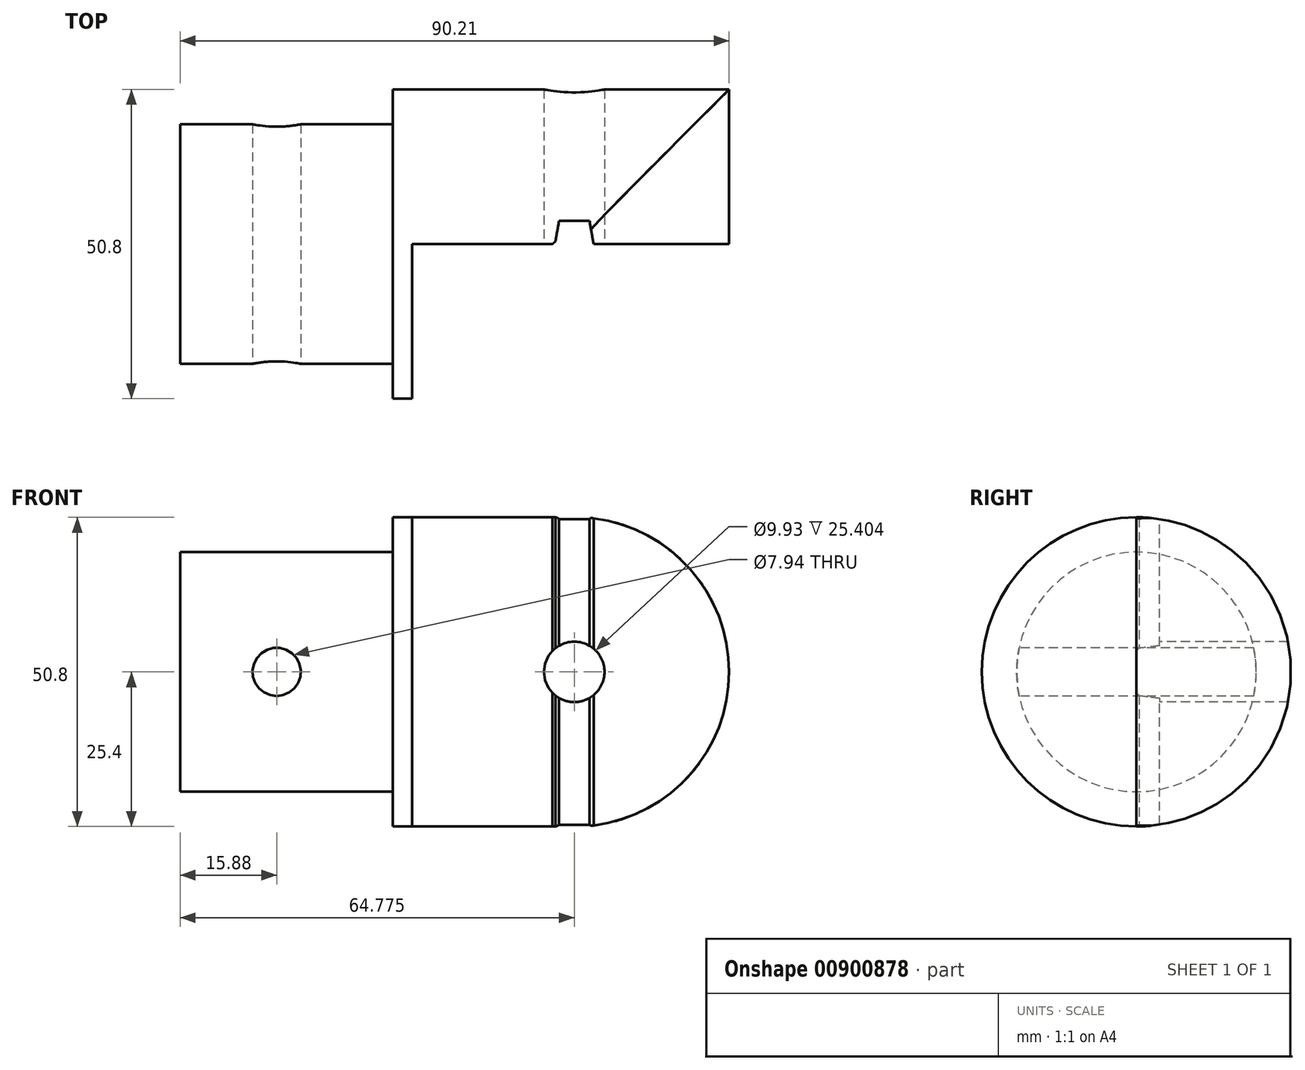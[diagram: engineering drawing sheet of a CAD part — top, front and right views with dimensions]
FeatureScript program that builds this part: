
annotation { "Feature Type Name" : "Feature", "Feature Type Description" : "" }
export const myFeature = defineFeature(function(context is Context, id is Id, definition is map)
    precondition{}
    {
        {
            var Q0;
            Q0=qCreatedBy(makeId("Right.planeOp"),FACE);
            var sketch = newSketch(context, id + "F0", { "sketchPlane" : qUnion([Q0])});
            skCircle(sketch, "E0", {"center": v(0, 0) * mm, "radius": 25.4 * mm});
            skSolve(sketch);
        }
        {
            var Q0;
            Q0=makeQuery(id+"F0.imprint","IMPRINT",FACE,{"disambiguationData":[TD([[makeQuery(id+"F0.imprint","IMPRINT",EDGE,{"derivedFrom":sQuery(id+"F0.wireOp",EDGE,"E0")}),1.0]])]});
            var Q1;
            Q1=sQuery(id+"F0.wireOp",EDGE,"E0");
            extrude(context, id + "F1", {"entities" : qUnion([Q0]), "surfaceEntities" : qUnion([Q1]), "depth" : 3.17 * mm, "offsetDistance" : 25.4 * mm});
        }
        {
            var Q0;
            Q0=makeQuery(id+"F1.opExtrude","CAP_FACE",FACE,{"disambiguationData":[OSD([sQuery(id+"F0.wireOp",EDGE,"E0")])],"isStart":false});
            var sketch = newSketch(context, id + "F2", { "sketchPlane" : qUnion([Q0])});
            skCircle(sketch, "E1", {"center": v(0, 0) * mm, "radius": 19.69 * mm});
            skSolve(sketch);
        }
        {
            var Q0;
            Q0 = qSketchRegion(id + "F2", true);
            extrude(context, id + "F3", {"entities" : qUnion([Q0]), "operationType" : NewBodyOperationType.ADD, "oppositeDirection" : true, "depth" : 38.1 * mm, "offsetDistance" : 25.4 * mm});
        }
        {
            var Q0;
            Q0=qCreatedBy(makeId("Right.planeOp"),FACE);
            var sketch = newSketch(context, id + "F4", { "sketchPlane" : qUnion([Q0])});
            skCircle(sketch, "E2.0", {"center": v(0, 0) * mm, "radius": 25.4 * mm});
            skSolve(sketch);
        }
        {
            var Q0;
            Q0 = qSketchRegion(id + "F4", true);
            extrude(context, id + "F5", {"entities" : qUnion([Q0]), "operationType" : NewBodyOperationType.ADD, "depth" : 58.42 * mm, "offsetDistance" : 25.4 * mm});
        }
        {
            var Q0;
            Q0=qCreatedBy(makeId("Front.planeOp"),FACE);
            var sketch = newSketch(context, id + "F6", { "sketchPlane" : qUnion([Q0])});
            skLineSegment(sketch, "E3", {"start": v(3.18, 25.4) * mm, "end": v(50.8, 25.4) * mm});
            skLineSegment(sketch, "E4", {"start": v(58.42, -25.4) * mm, "end": v(3.18, -25.4) * mm});
            skLineSegment(sketch, "E5.bottom", {"start": v(3.18, 25.4) * mm, "end": v(58.42, 25.4) * mm});
            skLineSegment(sketch, "E5.top", {"start": v(3.18, -25.4) * mm, "end": v(58.42, -25.4) * mm});
            skLineSegment(sketch, "E5.left", {"start": v(3.18, 25.4) * mm, "end": v(3.18, -25.4) * mm});
            skLineSegment(sketch, "E5.right", {"start": v(58.42, 25.4) * mm, "end": v(58.42, -25.4) * mm});
            skSolve(sketch);
        }
        {
            var Q0;
            Q0 = qSketchRegion(id + "F6", true);
            extrude(context, id + "F7", {"entities" : qUnion([Q0]), "operationType" : NewBodyOperationType.REMOVE, "endBound" : BoundingType.THROUGH_ALL, "depth" : 25.4 * mm, "offsetDistance" : 25.4 * mm});
        }
        {
            var Q0;
            Q0=makeQuery(id+"F7.boolean.opBoolean","COPY",FACE,{"derivedFrom":makeQuery(id+"F7.opExtrude","SWEPT_FACE",FACE,{"disambiguationData":[OSD([sQuery(id+"F6.wireOp",EDGE,"E5.left")])]})});
            cPlane(context, id + "F8", {"entities" : qUnion([Q0]), "cplaneType" : CPlaneType.OFFSET, "offset" : 26.67 * mm, "width" : 152.4 * mm, "height" : 152.4 * mm});
        }
        {
            var Q0;
            Q0=qCreatedBy(makeId("Front.planeOp"),FACE);
            var sketch = newSketch(context, id + "F9", { "sketchPlane" : qUnion([Q0])});
            skPoint(sketch, "E6", {"position": v(29.85, 0) * mm});
            skSolve(sketch);
        }
        {
            var Q0;
            Q0=sQuery(id+"F9.wireOp",VERTEX,"E6");
            var Q1;
            Q1=makeQuery(id+"F1.opExtrude","SWEPT_BODY",BODY,{"disambiguationData":[OSD([sQuery(id+"F0.wireOp",EDGE,"E0")])]});
            hole(context, id + "F10", {"style" : HoleStyle.SIMPLE, "endStyle" : HoleEndStyle.THROUGH, "standardTappedOrClearance" : lookupTablePath({ "fit" : "Close (ASME)", "standard" : "ANSI", "size" : "3/8", "type" : "Clearance" }), "standardBlindInLast" : lookupTablePath({ "fit" : "Close", "standard" : "ANSI", "size" : "3/8", "type" : "Clearance" }), "holeDiameter" : 9.93 * mm, "majorDiameter" : 9.52 * mm, "isTappedThrough" : true, "tappedDepth" : 12.7 * mm, "tapClearance" : 3, "locations" : qUnion([Q0]), "scope" : qUnion([Q1])});
        }
        {
            var Q0;
            Q0=qCreatedBy(makeId("Top.planeOp"),FACE);
            var sketch = newSketch(context, id + "F11", { "sketchPlane" : qUnion([Q0])});
            skLineSegment(sketch, "E7.left", {"start": v(26.67, 0) * mm, "end": v(33.02, 0) * mm});
            skLineSegment(sketch, "E7.right", {"start": v(27.34, 3.81) * mm, "end": v(32.35, 3.81) * mm});
            skLineSegment(sketch, "E8", {"start": v(26.67, 0) * mm, "end": v(27.34, 3.81) * mm});
            skLineSegment(sketch, "E9", {"start": v(33.02, 0) * mm, "end": v(32.35, 3.81) * mm});
            skLineSegment(sketch, "E10", {"start": v(29.85, 0) * mm, "end": v(29.85, 6.7) * mm, "construction": true});
            skSolve(sketch);
        }
        {
            var Q0;
            Q0 = qSketchRegion(id + "F11", true);
            var Q1;
            Q1=makeQuery(id+"F7.boolean.opBoolean","MERGE",FACE,{"derivedFrom":[makeQuery(id+"F1.opExtrude","CAP_FACE",FACE,{"disambiguationData":[OSD([sQuery(id+"F0.wireOp",EDGE,"E0")])],"isStart":false})],"fromTools":[makeQuery(id+"F7.opExtrude","SWEPT_FACE",FACE,{"disambiguationData":[OSD([sQuery(id+"F6.wireOp",EDGE,"E5.left")])]})]});
            extrude(context, id + "F12", {"entities" : qUnion([Q0]), "operationType" : NewBodyOperationType.REMOVE, "endBound" : BoundingType.SYMMETRIC, "oppositeDirection" : true, "depth" : 50.8 * mm, "endBoundEntityFace" : qUnion([Q1]), "offsetDistance" : 25.4 * mm});
        }
        {
            var Q0;
            Q0=qCreatedBy(makeId("Front.planeOp"),FACE);
            cPlane(context, id + "F13", {"entities" : qUnion([Q0]), "cplaneType" : CPlaneType.OFFSET, "offset" : 25.4 * mm, "width" : 152.4 * mm, "height" : 152.4 * mm});
        }
        {
            var Q0;
            Q0=qCreatedBy(id+"F13.planeOp",FACE);
            var sketch = newSketch(context, id + "F14", { "sketchPlane" : qUnion([Q0])});
            skPoint(sketch, "E11", {"position": v(29.85, 0) * mm});
            skPoint(sketch, "E12", {"position": v(29.85, 25.43) * mm});
            skArc(sketch, "E13", {"start": v(29.85, -25.43) * mm, "mid": v(55.28, 0) * mm, "end": v(29.85, 25.43) * mm});
            skLineSegment(sketch, "E14", {"start": v(58.42, -32.23) * mm, "end": v(58.42, 32.23) * mm});
            skLineSegment(sketch, "E15", {"start": v(58.42, 32.23) * mm, "end": v(29.85, 32.23) * mm});
            skLineSegment(sketch, "E16", {"start": v(29.85, 32.23) * mm, "end": v(29.85, 25.43) * mm});
            skLineSegment(sketch, "E17", {"start": v(29.85, -32.23) * mm, "end": v(29.85, -25.43) * mm});
            skLineSegment(sketch, "E18", {"start": v(29.85, 25.4) * mm, "end": v(29.85, -27.97) * mm, "construction": true});
            skLineSegment(sketch, "E19", {"start": v(29.85, -32.23) * mm, "end": v(58.42, -32.23) * mm});
            skLineSegment(sketch, "E20", {"start": v(-41.71, 0) * mm, "end": v(65, 0) * mm, "construction": true});
            skSolve(sketch);
        }
        {
            var Q0;
            Q0 = qSketchRegion(id + "F14", true);
            extrude(context, id + "F15", {"entities" : qUnion([Q0]), "operationType" : NewBodyOperationType.REMOVE, "endBound" : BoundingType.THROUGH_ALL, "oppositeDirection" : true, "depth" : 25.4 * mm, "offsetDistance" : 25.4 * mm});
        }
        {
            var Q0;
            Q0=makeQuery(id+"F12.boolean.opBoolean","COPY",EDGE,{"derivedFrom":makeQuery(id+"F12.opExtrude","SWEPT_EDGE",EDGE,{"disambiguationData":[OSD([sQuery(id+"F11.wireOp",EDGE,"E7.left"),sQuery(id+"F11.wireOp",EDGE,"E8")])]})});
            var Q1;
            Q1=makeQuery(id+"F12.boolean.opBoolean","COPY",EDGE,{"derivedFrom":makeQuery(id+"F12.opExtrude","SWEPT_EDGE",EDGE,{"disambiguationData":[OSD([sQuery(id+"F11.wireOp",EDGE,"E7.left"),sQuery(id+"F11.wireOp",EDGE,"E9")])]})});
            chamfer(context, id + "F16", {"entities" : qUnion([Q0, Q1]), "width" : 0.5 * mm, "tangentPropagation" : true});
        }
        {
            var Q0;
            Q0=qCreatedBy(id+"F13.planeOp",FACE);
            var sketch = newSketch(context, id + "F17", { "sketchPlane" : qUnion([Q0])});
            skPoint(sketch, "E21", {"position": v(-19.05, 0) * mm});
            skSolve(sketch);
        }
        {
            var Q0;
            Q0=sQuery(id+"F17.wireOp",VERTEX,"E21");
            var Q1;
            Q1=makeQuery(id+"F1.opExtrude","SWEPT_BODY",BODY,{"disambiguationData":[OSD([sQuery(id+"F0.wireOp",EDGE,"E0")])]});
            hole(context, id + "F18", {"style" : HoleStyle.SIMPLE, "endStyle" : HoleEndStyle.THROUGH, "standardTappedOrClearance" : lookupTablePath({ "standard" : "ANSI", "engagement" : "75%", "pitch" : "16 tpi", "size" : "3/8", "type" : "Tapped" }), "standardBlindInLast" : lookupTablePath({ "standard" : "ANSI", "engagement" : "75%", "pitch" : "16 tpi", "size" : "3/8", "type" : "Tapped" }), "holeDiameter" : 7.94 * mm, "majorDiameter" : 9.52 * mm, "showTappedDepth" : true, "isTappedThrough" : true, "tappedDepth" : 12.7 * mm, "tapClearance" : 3, "locations" : qUnion([Q0]), "scope" : qUnion([Q1])});
        }
    });
